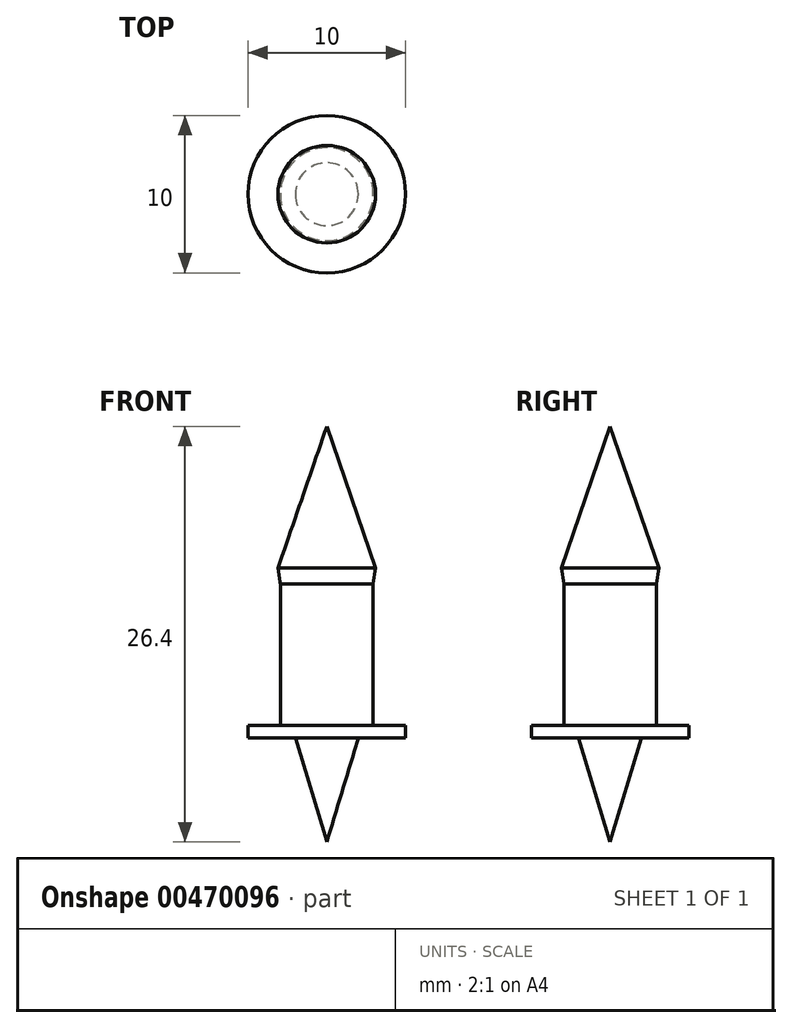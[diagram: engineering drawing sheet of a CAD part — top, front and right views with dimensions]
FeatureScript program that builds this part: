
annotation { "Feature Type Name" : "Feature", "Feature Type Description" : "" }
export const myFeature = defineFeature(function(context is Context, id is Id, definition is map)
    precondition{}
    {
        {
            var Q0;
            Q0=qCreatedBy(makeId("Front.planeOp"),FACE);
            var sketch = newSketch(context, id + "F0", { "sketchPlane" : qUnion([Q0])});
            skLineSegment(sketch, "E0", {"start": v(0, -6.6) * mm, "end": v(-2, 0) * mm});
            skLineSegment(sketch, "E1", {"start": v(-2, 0) * mm, "end": v(-5, 0) * mm});
            skLineSegment(sketch, "E2", {"start": v(-5, 0) * mm, "end": v(-5, 0.8) * mm});
            skLineSegment(sketch, "E3", {"start": v(-5, 0.8) * mm, "end": v(-2.95, 0.8) * mm});
            skLineSegment(sketch, "E4", {"start": v(-2.95, 0.8) * mm, "end": v(-2.95, 9.8) * mm});
            skLineSegment(sketch, "E5", {"start": v(-2.95, 9.8) * mm, "end": v(-3.1, 10.8) * mm});
            skLineSegment(sketch, "E6", {"start": v(-3.1, 10.8) * mm, "end": v(0, 19.8) * mm});
            skLineSegment(sketch, "E7", {"start": v(0, 19.8) * mm, "end": v(0, -6.6) * mm});
            skLineSegment(sketch, "E8", {"start": v(0, 19.8) * mm, "end": v(0, 25.6) * mm, "construction": true});
            skSolve(sketch);
        }
        {
            var Q0;
            Q0=makeQuery(id+"F0.imprint","IMPRINT",FACE,{"disambiguationData":[TD([[makeQuery(id+"F0.imprint","IMPRINT",EDGE,{"derivedFrom":sQuery(id+"F0.wireOp",EDGE,"E0")}),-1.0]])]});
            var Q1;
            Q1=sQuery(id+"F0.wireOp",EDGE,"E8");
            revolve(context, id + "F1", {"entities" : qUnion([Q0]), "axis" : qUnion([Q1]), "revolveType" : RevolveType.FULL});
        }
    });
